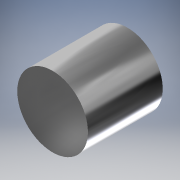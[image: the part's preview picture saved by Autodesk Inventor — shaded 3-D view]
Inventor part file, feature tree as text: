
AUTODESK INVENTOR PART (.ipt)
format: ipt  version: 2017 (Build 210142000, 142)  size: 108,032 bytes
history: native  units: mm
features: extrude x1, shell x1, sketch x1
ambient origin geometry x8: Origin, YZ Plane, XZ Plane, XY Plane, X Axis, Y Axis, Z Axis, Center Point
bodies: Solid1 (feature_tree)
feature tree (3):
  extrude  "Extrusion1"  Depth=180.0mm TaperAngle=0.0deg
  shell  "Shell1"  Thickness=2.0mm
  sketch  "Sketch1"  dims[d0=170.0mm d1=180.0mm d2=0.0mm d3=2.0mm]
